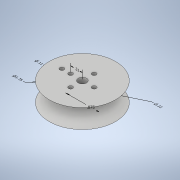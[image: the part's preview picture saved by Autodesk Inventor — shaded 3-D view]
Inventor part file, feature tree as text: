
AUTODESK INVENTOR PART (.ipt)
format: ipt  version: 2020 (Build 240168000, 168)  size: 165,888 bytes
history: native  units: in
note: dims shown in document units (in); Inventor stores cm internally (conversion verified against a paired STEP export)
features: sketch x4, extrude x3, chamfer x2
ambient origin geometry x8: Origin, YZ Plane, XZ Plane, XY Plane, X Axis, Y Axis, Z Axis, Center Point
bodies: Solid1 (feature_tree)
feature tree (9):
  extrude  "Extrusion1"  Depth=0.25in TaperAngle=0.0deg
  chamfer  "Chamfer1"  Distance=0.5in Angle=45.0deg
  extrude  "Extrusion2"  Depth=0.5in TaperAngle=45.0deg
  chamfer  "Chamfer2"  Distance=0.23in
  extrude  "Extrusion3"  Depth=0.31in
  sketch  "Sketch5"  dims[d29=0.31in d30=0.23in d31=0.31in d32=0.31in d33=0.31in d34=0.11in d35=0.11in d36=0.11in d37=0.11in d38=0.11in d39=0.6in d40=0.0in d57=1.75in d58=0.875in d26=1.5792in d27=1.75in d41=0.3293in d42=1.75in d43=1.4463in d44=0.1321in d45=0.0594in d46=0.22in d47=0.0541in d48=0.0954in d49=0.31in d50=0.0598in d51=0.0586in d52=0.23in d53=-0.3764in d54=0.0667in d55=0.0375in d56=0.11in]
  sketch  "Sketch1"  dims[d0=1.75in d1=0.25in d2=0.0in d7=0.5in d8=0.25in d9=45.0deg]
  sketch  "Sketch2"  dims[d10=0.25in d11=0.0in d12=0.5in d13=0.25in d14=45.0deg]
  sketch  "Sketch4"  dims[d28=0.22in]
